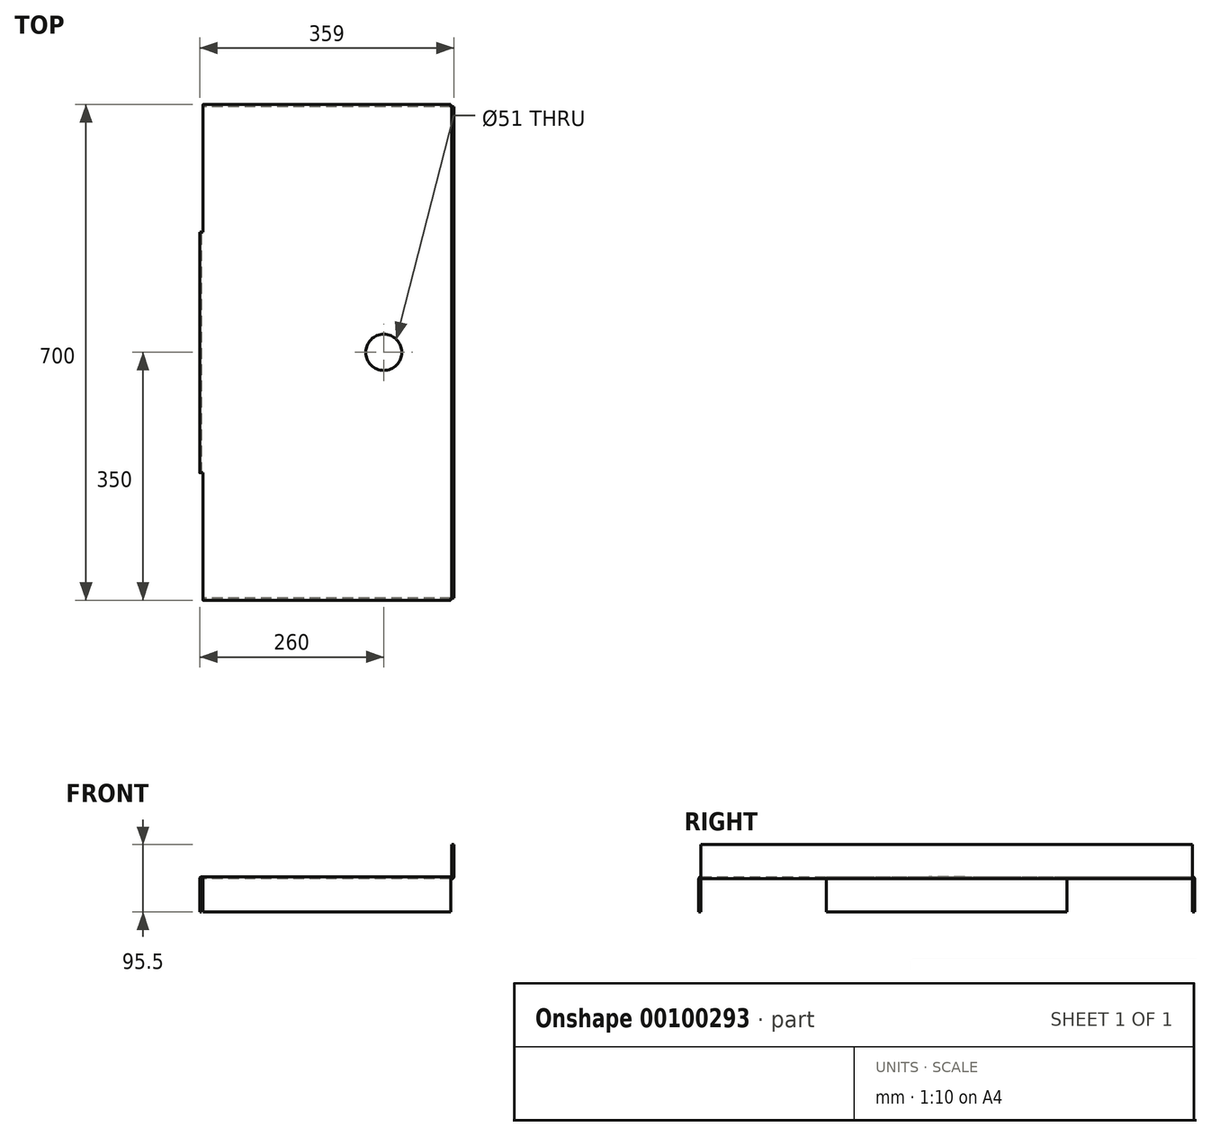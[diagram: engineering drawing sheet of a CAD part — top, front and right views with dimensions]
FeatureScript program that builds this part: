
annotation { "Feature Type Name" : "Feature", "Feature Type Description" : "" }
export const myFeature = defineFeature(function(context is Context, id is Id, definition is map)
    precondition{}
    {
        {
            var Q0;
            Q0=qCreatedBy(makeId("Right.planeOp"),FACE);
            var sketch = newSketch(context, id + "F0", { "sketchPlane" : qUnion([Q0])});
            skLineSegment(sketch, "E0", {"start": v(-350, 1.5) * mm, "end": v(-350, -45.5) * mm});
            skLineSegment(sketch, "E1", {"start": v(-345.5, 1.5) * mm, "end": v(345.5, 1.5) * mm});
            skLineSegment(sketch, "E2", {"start": v(350, -45.5) * mm, "end": v(350, 1.5) * mm});
            skLineSegment(sketch, "E3", {"start": v(-350, -45.5) * mm, "end": v(350, -45.5) * mm, "construction": true});
            skLineSegment(sketch, "E4", {"start": v(-350, -45.5) * mm, "end": v(-347, -45.5) * mm});
            skLineSegment(sketch, "E5", {"start": v(-347, 0) * mm, "end": v(-347, -45.5) * mm});
            skLineSegment(sketch, "E6", {"start": v(-347, 4.5) * mm, "end": v(347, 4.5) * mm});
            skLineSegment(sketch, "E7", {"start": v(347, -45.5) * mm, "end": v(347, 0) * mm});
            skLineSegment(sketch, "E8", {"start": v(347, -45.5) * mm, "end": v(350, -45.5) * mm});
            skPoint(sketch, "E9.visualSharp", {"position": v(-347, 1.5) * mm});
            skArc(sketch, "E9.filletArc", {"start": v(-345.5, 1.5) * mm, "mid": v(-346.56, 1.06) * mm, "end": v(-347, 0) * mm});
            skPoint(sketch, "E10.visualSharp", {"position": v(-350, 4.5) * mm});
            skArc(sketch, "E10.filletArc", {"start": v(-347, 4.5) * mm, "mid": v(-349.12, 3.62) * mm, "end": v(-350, 1.5) * mm});
            skPoint(sketch, "E11.visualSharp", {"position": v(350, 4.5) * mm});
            skArc(sketch, "E11.filletArc", {"start": v(350, 1.5) * mm, "mid": v(349.12, 3.62) * mm, "end": v(347, 4.5) * mm});
            skArc(sketch, "E12.filletArc", {"start": v(347, 0) * mm, "mid": v(346.56, 1.06) * mm, "end": v(345.5, 1.5) * mm});
            skSolve(sketch);
        }
        {
            var Q0;
            Q0 = qSketchRegion(id + "F0", true);
            extrude(context, id + "F1", {"entities" : qUnion([Q0]), "depth" : 100 * mm, "hasSecondDirection" : true, "secondDirectionOppositeDirection" : true, "secondDirectionDepth" : 250 * mm});
        }
        {
            var Q0;
            Q0=qCreatedBy(makeId("Front.planeOp"),FACE);
            var sketch = newSketch(context, id + "F2", { "sketchPlane" : qUnion([Q0])});
            skLineSegment(sketch, "E13.0.3", {"start": v(-251.5, 4.5) * mm, "end": v(-250, 4.5) * mm});
            skLineSegment(sketch, "E14", {"start": v(-254.5, 1.5) * mm, "end": v(-254.5, -45.5) * mm});
            skLineSegment(sketch, "E15", {"start": v(-254.5, -45.5) * mm, "end": v(-251.5, -45.5) * mm});
            skLineSegment(sketch, "E16", {"start": v(-251.5, -45.5) * mm, "end": v(-251.5, 0) * mm});
            skArc(sketch, "E17.filletArc", {"start": v(-251.5, 4.5) * mm, "mid": v(-253.62, 3.62) * mm, "end": v(-254.5, 1.5) * mm});
            skLineSegment(sketch, "E18.0", {"start": v(-250, 4.5) * mm, "end": v(-250, 1.5) * mm});
            skLineSegment(sketch, "E19", {"start": v(-250, 1.5) * mm, "end": v(-250, 1.5) * mm});
            skArc(sketch, "E20.filletArc", {"start": v(-250, 1.5) * mm, "mid": v(-251.06, 1.06) * mm, "end": v(-251.5, 0) * mm});
            skSolve(sketch);
        }
        {
            var Q0;
            Q0=makeQuery(id+"F2.imprint","IMPRINT",FACE,{"disambiguationData":[TD([[makeQuery(id+"F2.imprint","IMPRINT",EDGE,{"derivedFrom":sQuery(id+"F2.wireOp",EDGE,"E13.0.3")}),1.0]])]});
            var Q1;
            Q1=makeQuery(id+"F2.imprint","IMPRINT",FACE,{"disambiguationData":[TD([[makeQuery(id+"F2.imprint","IMPRINT",EDGE,{"derivedFrom":sQuery(id+"F2.wireOp",EDGE,"E13.0.3")}),-1.0]])]});
            extrude(context, id + "F3", {"entities" : qUnion([Q0, Q1]), "operationType" : NewBodyOperationType.ADD, "endBound" : BoundingType.SYMMETRIC, "depth" : 340 * mm});
        }
        {
            var Q0;
            Q0=qCreatedBy(makeId("Front.planeOp"),FACE);
            var sketch = newSketch(context, id + "F4", { "sketchPlane" : qUnion([Q0])});
            skLineSegment(sketch, "E21", {"start": v(101.5, 50) * mm, "end": v(104.5, 50) * mm});
            skLineSegment(sketch, "E22", {"start": v(104.5, 50) * mm, "end": v(104.5, 4.5) * mm});
            skLineSegment(sketch, "E23", {"start": v(101.5, 50) * mm, "end": v(101.5, 6) * mm});
            skArc(sketch, "E24.filletArc", {"start": v(100, 4.5) * mm, "mid": v(101.06, 4.94) * mm, "end": v(101.5, 6) * mm});
            skArc(sketch, "E25.filletArc", {"start": v(101.5, 1.5) * mm, "mid": v(103.62, 2.38) * mm, "end": v(104.5, 4.5) * mm});
            skLineSegment(sketch, "E26", {"start": v(100, 4.5) * mm, "end": v(100, 1.5) * mm});
            skLineSegment(sketch, "E27", {"start": v(101.5, 1.5) * mm, "end": v(100, 1.5) * mm});
            skSolve(sketch);
        }
        {
            var Q0;
            Q0 = qSketchRegion(id + "F4", true);
            extrude(context, id + "F5", {"entities" : qUnion([Q0]), "operationType" : NewBodyOperationType.ADD, "depth" : 347 * mm, "hasSecondDirection" : true, "secondDirectionOppositeDirection" : true, "secondDirectionDepth" : 347 * mm});
        }
        {
            var Q0;
            Q0=qCreatedBy(makeId("Top.planeOp"),FACE);
            var sketch = newSketch(context, id + "F6", { "sketchPlane" : qUnion([Q0])});
            skCircle(sketch, "E28", {"center": v(5.5, 0) * mm, "radius": 25.5 * mm});
            skSolve(sketch);
        }
        {
            var Q0;
            Q0 = qSketchRegion(id + "F6", true);
            extrude(context, id + "F7", {"entities" : qUnion([Q0]), "operationType" : NewBodyOperationType.REMOVE, "depth" : 25 * mm});
        }
    });
